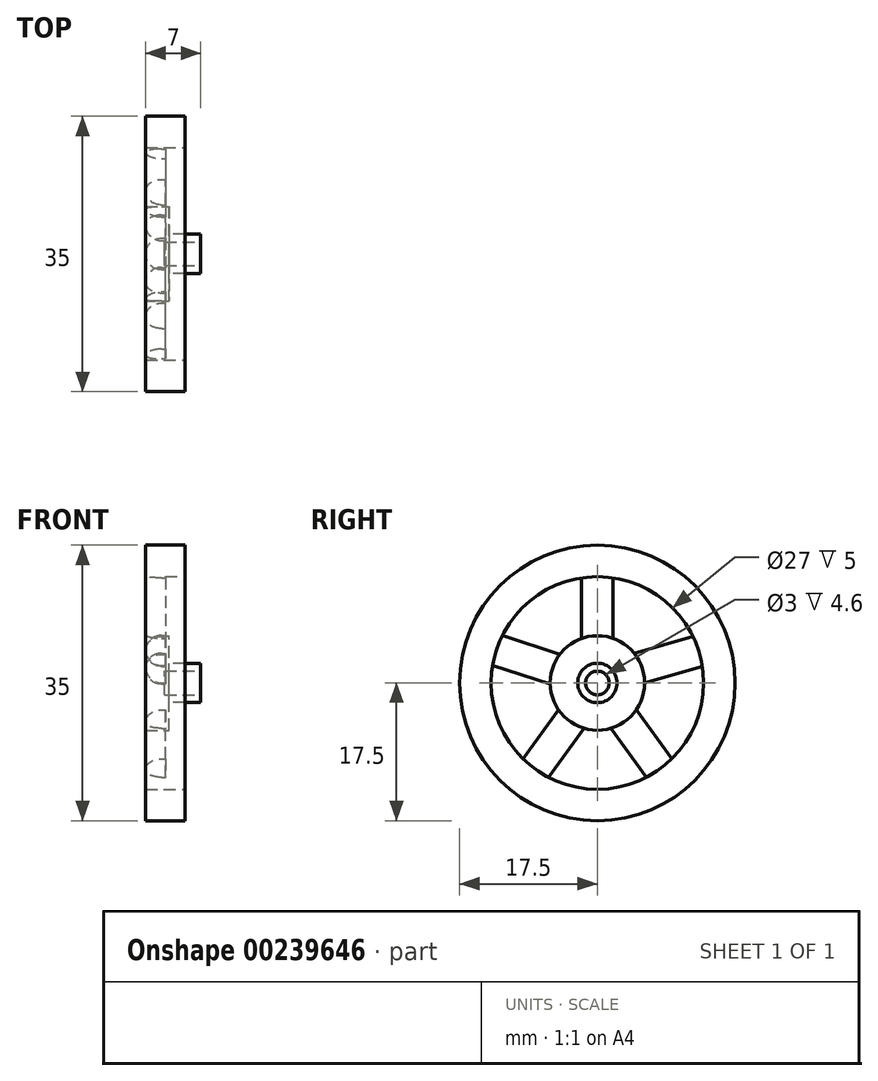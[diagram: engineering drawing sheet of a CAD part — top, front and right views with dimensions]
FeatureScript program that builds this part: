
annotation { "Feature Type Name" : "Feature", "Feature Type Description" : "" }
export const myFeature = defineFeature(function(context is Context, id is Id, definition is map)
    precondition{}
    {
        {
            var Q0;
            Q0=qCreatedBy(makeId("Right.planeOp"),FACE);
            var sketch = newSketch(context, id + "F0", { "sketchPlane" : qUnion([Q0])});
            skCircle(sketch, "E0", {"center": v(0, 0) * mm, "radius": 17.5 * mm});
            skSolve(sketch);
        }
        {
            var Q0;
            Q0 = qSketchRegion(id + "F0", true);
            extrude(context, id + "F1", {"entities" : qUnion([Q0]), "depth" : 5 * mm});
        }
        {
            var Q0;
            Q0=makeQuery(id+"F1.opExtrude","CAP_FACE",FACE,{"disambiguationData":[OSD([sQuery(id+"F0.wireOp",EDGE,"E0")])],"isStart":false});
            var sketch = newSketch(context, id + "F2", { "sketchPlane" : qUnion([Q0])});
            skCircle(sketch, "E1", {"center": v(0, 0) * mm, "radius": 13.5 * mm});
            skCircle(sketch, "E2", {"center": v(0, 0) * mm, "radius": 6 * mm});
            skLineSegment(sketch, "E3", {"start": v(0, 0) * mm, "end": v(0, 13.5) * mm});
            skLineSegment(sketch, "E4", {"start": v(0, 0) * mm, "end": v(12.84, 4.17) * mm});
            skLineSegment(sketch, "E5", {"start": v(0, 0) * mm, "end": v(7.94, -10.92) * mm});
            skLineSegment(sketch, "E6", {"start": v(0, 0) * mm, "end": v(-7.94, -10.92) * mm});
            skLineSegment(sketch, "E7", {"start": v(0, 0) * mm, "end": v(-12.84, 4.17) * mm});
            skLineSegment(sketch, "E8", {"start": v(2, 5.66) * mm, "end": v(2, 13.35) * mm});
            skLineSegment(sketch, "E9", {"start": v(-2, 5.66) * mm, "end": v(-2, 13.35) * mm});
            skLineSegment(sketch, "E10", {"start": v(4.66, 3.78) * mm, "end": v(12.13, 5.93) * mm});
            skLineSegment(sketch, "E11", {"start": v(6, 0) * mm, "end": v(13.33, 2.12) * mm});
            skLineSegment(sketch, "E12", {"start": v(4.94, -3.4) * mm, "end": v(9.47, -9.63) * mm});
            skLineSegment(sketch, "E13", {"start": v(1.7, -5.75) * mm, "end": v(6.23, -11.98) * mm});
            skLineSegment(sketch, "E14", {"start": v(-1.7, -5.75) * mm, "end": v(-6.23, -11.98) * mm});
            skLineSegment(sketch, "E15", {"start": v(-4.94, -3.4) * mm, "end": v(-9.47, -9.63) * mm});
            skLineSegment(sketch, "E16", {"start": v(-6, -0.15) * mm, "end": v(-13.32, 2.22) * mm});
            skLineSegment(sketch, "E17", {"start": v(-4.76, 3.65) * mm, "end": v(-12.08, 6.03) * mm});
            skLineSegment(sketch, "E18", {"start": v(-2, 10.59) * mm, "end": v(0, 10.59) * mm, "construction": true});
            skLineSegment(sketch, "E19", {"start": v(0, 10.59) * mm, "end": v(2, 10.59) * mm, "construction": true});
            skLineSegment(sketch, "E20", {"start": v(9.03, 5.04) * mm, "end": v(9.65, 3.13) * mm, "construction": true});
            skLineSegment(sketch, "E21", {"start": v(9.65, 3.13) * mm, "end": v(10.2, 1.21) * mm, "construction": true});
            skLineSegment(sketch, "E22", {"start": v(-9.08, 2.95) * mm, "end": v(-8.46, 4.85) * mm, "construction": true});
            skLineSegment(sketch, "E23", {"start": v(-10, 1.15) * mm, "end": v(-9.38, 3.05) * mm, "construction": true});
            skLineSegment(sketch, "E24", {"start": v(6.15, -8.47) * mm, "end": v(7.77, -7.3) * mm});
            skLineSegment(sketch, "E25", {"start": v(6.15, -8.47) * mm, "end": v(4.54, -9.64) * mm});
            skLineSegment(sketch, "E26", {"start": v(-5.61, -7.73) * mm, "end": v(-4, -8.9) * mm, "construction": true});
            skLineSegment(sketch, "E27", {"start": v(-6.78, -5.93) * mm, "end": v(-5.16, -7.1) * mm, "construction": true});
            skSolve(sketch);
        }
        {
            var Q0;
            {var subQ0=sQuery(id+"F2.wireOp",EDGE,"E9");Q0=makeQuery(id+"F2.imprint","IMPRINT",FACE,{"disambiguationData":[TD([[makeQuery(id+"F2.imprint","IMPRINT",EDGE,{"derivedFrom":subQ0}),1.0]])]});}
            var Q1;
            {var subQ0=sQuery(id+"F2.wireOp",EDGE,"E8");Q1=makeQuery(id+"F2.imprint","IMPRINT",FACE,{"disambiguationData":[TD([[makeQuery(id+"F2.imprint","IMPRINT",EDGE,{"derivedFrom":subQ0}),-1.0]])]});}
            var Q2;
            {var subQ4=sQuery(id+"F2.wireOp",EDGE,"E11");Q2=makeQuery(id+"F2.imprint","IMPRINT",FACE,{"disambiguationData":[TD([[makeQuery(id+"F2.imprint","IMPRINT",EDGE,{"derivedFrom":subQ4}),-1.0]])]});}
            var Q3;
            {var subQ6=sQuery(id+"F2.wireOp",EDGE,"E14");Q3=makeQuery(id+"F2.imprint","IMPRINT",FACE,{"disambiguationData":[TD([[makeQuery(id+"F2.imprint","IMPRINT",EDGE,{"derivedFrom":subQ6}),1.0]])]});}
            var Q4;
            {var subQ0=sQuery(id+"F2.wireOp",EDGE,"E15");Q4=makeQuery(id+"F2.imprint","IMPRINT",FACE,{"disambiguationData":[TD([[makeQuery(id+"F2.imprint","IMPRINT",EDGE,{"derivedFrom":subQ0}),-1.0]])]});}
            extrude(context, id + "F3", {"entities" : qUnion([Q0, Q1, Q2, Q3, Q4]), "operationType" : NewBodyOperationType.REMOVE, "oppositeDirection" : true, "depth" : 25 * mm});
        }
        {
            var Q0;
            Q0=makeQuery(id+"F1.opExtrude","CAP_FACE",FACE,{"disambiguationData":[OSD([sQuery(id+"F0.wireOp",EDGE,"E0")])],"isStart":false});
            var sketch = newSketch(context, id + "F4", { "sketchPlane" : qUnion([Q0])});
            skCircle(sketch, "E28", {"center": v(0, 0) * mm, "radius": 13.5 * mm});
            skSolve(sketch);
        }
        {
            var Q0;
            Q0 = qSketchRegion(id + "F4", true);
            extrude(context, id + "F5", {"entities" : qUnion([Q0]), "operationType" : NewBodyOperationType.REMOVE, "oppositeDirection" : true, "depth" : 2.5 * mm});
        }
        {
            var Q0;
            Q0=makeQuery(id+"F3.boolean.opBoolean","INTERSECT",EDGE,{"derivedFrom":[makeQuery(id+"F1.opExtrude","CAP_FACE",FACE,{"disambiguationData":[OSD([sQuery(id+"F0.wireOp",EDGE,"E0")])],"isStart":true}),makeQuery(id+"F3.opExtrude","SWEPT_FACE",FACE,{"disambiguationData":[OSD([sQuery(id+"F2.wireOp",EDGE,"E16")])]})]});
            var Q1;
            Q1=makeQuery(id+"F3.boolean.opBoolean","INTERSECT",EDGE,{"derivedFrom":[makeQuery(id+"F1.opExtrude","CAP_FACE",FACE,{"disambiguationData":[OSD([sQuery(id+"F0.wireOp",EDGE,"E0")])],"isStart":true}),makeQuery(id+"F3.opExtrude","SWEPT_FACE",FACE,{"disambiguationData":[OSD([sQuery(id+"F2.wireOp",EDGE,"E17")])]})]});
            var Q2;
            Q2=makeQuery(id+"F3.boolean.opBoolean","INTERSECT",EDGE,{"derivedFrom":[makeQuery(id+"F1.opExtrude","CAP_FACE",FACE,{"disambiguationData":[OSD([sQuery(id+"F0.wireOp",EDGE,"E0")])],"isStart":true}),makeQuery(id+"F3.opExtrude","SWEPT_FACE",FACE,{"disambiguationData":[OSD([sQuery(id+"F2.wireOp",EDGE,"E15")])]})]});
            var Q3;
            Q3=makeQuery(id+"F3.boolean.opBoolean","INTERSECT",EDGE,{"derivedFrom":[makeQuery(id+"F1.opExtrude","CAP_FACE",FACE,{"disambiguationData":[OSD([sQuery(id+"F0.wireOp",EDGE,"E0")])],"isStart":true}),makeQuery(id+"F3.opExtrude","SWEPT_FACE",FACE,{"disambiguationData":[OSD([sQuery(id+"F2.wireOp",EDGE,"E14")])]})]});
            var Q4;
            Q4=makeQuery(id+"F3.boolean.opBoolean","INTERSECT",EDGE,{"derivedFrom":[makeQuery(id+"F1.opExtrude","CAP_FACE",FACE,{"disambiguationData":[OSD([sQuery(id+"F0.wireOp",EDGE,"E0")])],"isStart":true}),makeQuery(id+"F3.opExtrude","SWEPT_FACE",FACE,{"disambiguationData":[OSD([sQuery(id+"F2.wireOp",EDGE,"E13")])]})]});
            var Q5;
            Q5=makeQuery(id+"F3.boolean.opBoolean","INTERSECT",EDGE,{"derivedFrom":[makeQuery(id+"F1.opExtrude","CAP_FACE",FACE,{"disambiguationData":[OSD([sQuery(id+"F0.wireOp",EDGE,"E0")])],"isStart":true}),makeQuery(id+"F3.opExtrude","SWEPT_FACE",FACE,{"disambiguationData":[OSD([sQuery(id+"F2.wireOp",EDGE,"E12")])]})]});
            var Q6;
            Q6=makeQuery(id+"F3.boolean.opBoolean","INTERSECT",EDGE,{"derivedFrom":[makeQuery(id+"F1.opExtrude","CAP_FACE",FACE,{"disambiguationData":[OSD([sQuery(id+"F0.wireOp",EDGE,"E0")])],"isStart":true}),makeQuery(id+"F3.opExtrude","SWEPT_FACE",FACE,{"disambiguationData":[OSD([sQuery(id+"F2.wireOp",EDGE,"E11")])]})]});
            var Q7;
            Q7=makeQuery(id+"F3.boolean.opBoolean","INTERSECT",EDGE,{"derivedFrom":[makeQuery(id+"F1.opExtrude","CAP_FACE",FACE,{"disambiguationData":[OSD([sQuery(id+"F0.wireOp",EDGE,"E0")])],"isStart":true}),makeQuery(id+"F3.opExtrude","SWEPT_FACE",FACE,{"disambiguationData":[OSD([sQuery(id+"F2.wireOp",EDGE,"E8")])]})]});
            var Q8;
            Q8=makeQuery(id+"F3.boolean.opBoolean","INTERSECT",EDGE,{"derivedFrom":[makeQuery(id+"F1.opExtrude","CAP_FACE",FACE,{"disambiguationData":[OSD([sQuery(id+"F0.wireOp",EDGE,"E0")])],"isStart":true}),makeQuery(id+"F3.opExtrude","SWEPT_FACE",FACE,{"disambiguationData":[OSD([sQuery(id+"F2.wireOp",EDGE,"E9")])]})]});
            fillet(context, id + "F6", {"entities" : qUnion([Q0, Q1, Q2, Q3, Q4, Q5, Q6, Q7, Q8]), "radius" : 2 * mm, "tangentPropagation" : true, "allowEdgeOverflow" : false});
        }
        {
            var Q0;
            Q0=makeQuery(id+"F3.boolean.opBoolean","INTERSECT",EDGE,{"derivedFrom":[makeQuery(id+"F1.opExtrude","CAP_FACE",FACE,{"disambiguationData":[OSD([sQuery(id+"F0.wireOp",EDGE,"E0")])],"isStart":true}),makeQuery(id+"F3.opExtrude","SWEPT_FACE",FACE,{"disambiguationData":[OSD([sQuery(id+"F2.wireOp",EDGE,"E10")])]})]});
            fillet(context, id + "F7", {"entities" : qUnion([Q0]), "radius" : 2 * mm, "tangentPropagation" : true, "allowEdgeOverflow" : false});
        }
        {
            var Q0;
            Q0=makeQuery(id+"F5.boolean.opBoolean","COPY",FACE,{"derivedFrom":makeQuery(id+"F5.opExtrude","CAP_FACE",FACE,{"disambiguationData":[OSD([sQuery(id+"F4.wireOp",EDGE,"E28")])],"isStart":false})});
            var sketch = newSketch(context, id + "F8", { "sketchPlane" : qUnion([Q0])});
            skCircle(sketch, "E29", {"center": v(0, 0) * mm, "radius": 6 * mm});
            skSolve(sketch);
        }
        {
            var Q0;
            Q0 = qSketchRegion(id + "F8", true);
            extrude(context, id + "F9", {"entities" : qUnion([Q0]), "operationType" : NewBodyOperationType.ADD, "depth" : 0.5 * mm});
        }
        {
            var Q0;
            Q0=makeQuery(id+"F9.opExtrude","CAP_FACE",FACE,{"disambiguationData":[OSD([sQuery(id+"F8.wireOp",EDGE,"E29")])],"isStart":false});
            var sketch = newSketch(context, id + "F10", { "sketchPlane" : qUnion([Q0])});
            skCircle(sketch, "E30", {"center": v(0, 0) * mm, "radius": 2.5 * mm});
            skSolve(sketch);
        }
        {
            var Q0;
            Q0 = qSketchRegion(id + "F10", true);
            extrude(context, id + "F11", {"entities" : qUnion([Q0]), "operationType" : NewBodyOperationType.ADD, "depth" : 4 * mm});
        }
        {
            var Q0;
            Q0=makeQuery(id+"F11.opExtrude","CAP_FACE",FACE,{"disambiguationData":[OSD([sQuery(id+"F10.wireOp",EDGE,"E30")])],"isStart":false});
            var sketch = newSketch(context, id + "F12", { "sketchPlane" : qUnion([Q0])});
            skCircle(sketch, "E31", {"center": v(0, 0) * mm, "radius": 1.5 * mm});
            skSolve(sketch);
        }
        {
            var Q0;
            Q0 = qSketchRegion(id + "F12", true);
            extrude(context, id + "F13", {"entities" : qUnion([Q0]), "operationType" : NewBodyOperationType.REMOVE, "oppositeDirection" : true, "depth" : 4.6 * mm});
        }
    });
